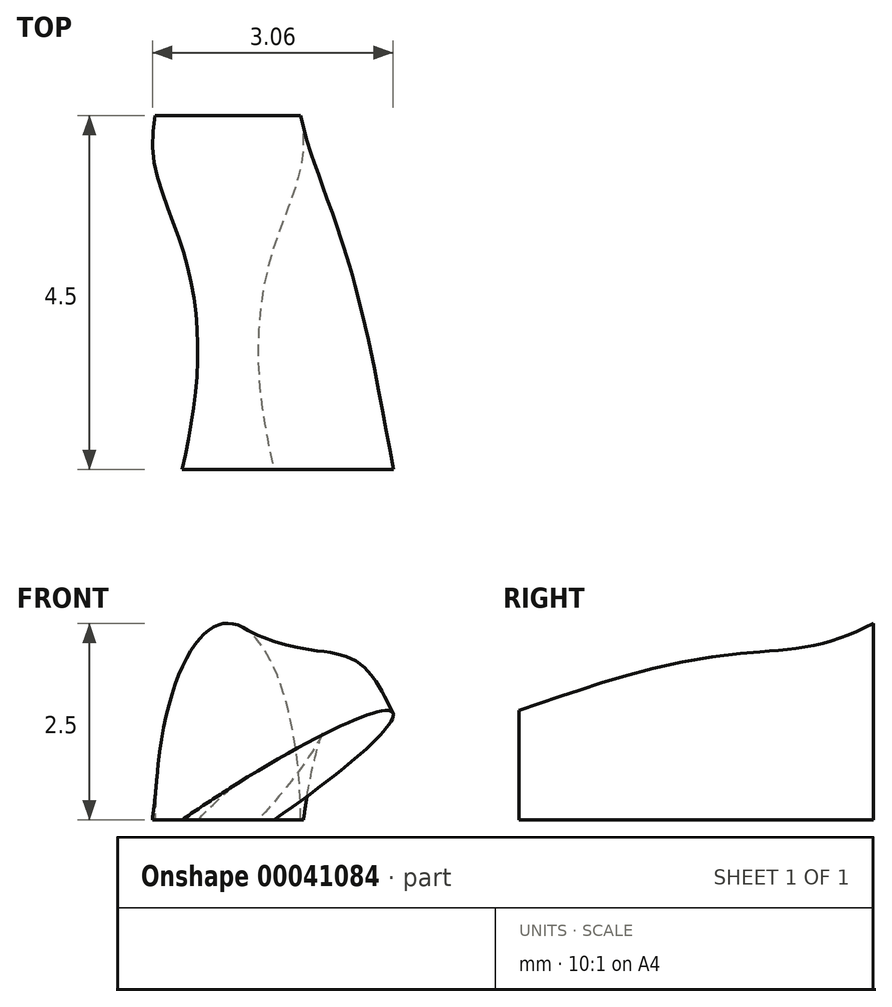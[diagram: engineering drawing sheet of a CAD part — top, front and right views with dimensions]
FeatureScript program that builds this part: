
annotation { "Feature Type Name" : "Feature", "Feature Type Description" : "" }
export const myFeature = defineFeature(function(context is Context, id is Id, definition is map)
    precondition{}
    {
        {
            var Q0;
            Q0=qCreatedBy(makeId("Front.planeOp"),FACE);
            cPlane(context, id + "F0", {"entities" : qUnion([Q0]), "cplaneType" : CPlaneType.OFFSET, "offset" : 1.5 * mm, "width" : 150 * mm, "height" : 150 * mm});
        }
        {
            var Q0;
            Q0=qCreatedBy(makeId("Front.planeOp"),FACE);
            cPlane(context, id + "F1", {"entities" : qUnion([Q0]), "cplaneType" : CPlaneType.OFFSET, "offset" : 4.5 * mm, "width" : 150 * mm, "height" : 150 * mm});
        }
        {
            var Q0;
            Q0=qCreatedBy(makeId("Front.planeOp"),FACE);
            var sketch = newSketch(context, id + "F2", { "sketchPlane" : qUnion([Q0])});
            skEllipse(sketch, "E0", {"center": v(0, 0) * mm, "majorRadius": 2.5 * mm, "minorRadius": 0.92 * mm, "majorAxis": v(0, 1)});
            skSolve(sketch);
        }
        {
            var Q0;
            Q0=qCreatedBy(id+"F0.planeOp",FACE);
            var sketch = newSketch(context, id + "F3", { "sketchPlane" : qUnion([Q0])});
            skEllipse(sketch, "E1", {"center": v(0, 0) * mm, "majorRadius": 2.5 * mm, "minorRadius": 0.55 * mm, "majorAxis": v(0.54, 0.84)});
            skSolve(sketch);
        }
        {
            var Q0;
            Q0=qCreatedBy(id+"F1.planeOp",FACE);
            var sketch = newSketch(context, id + "F4", { "sketchPlane" : qUnion([Q0])});
            skEllipse(sketch, "E2", {"center": v(0, 0) * mm, "majorRadius": 2.5 * mm, "minorRadius": 0.33 * mm, "majorAxis": v(0.84, 0.55)});
            skSolve(sketch);
        }
        {
            var Q0;
            Q0=makeQuery(id+"F2.imprint","IMPRINT",FACE,{"disambiguationData":[TD([[makeQuery(id+"F2.imprint","IMPRINT",EDGE,{"derivedFrom":sQuery(id+"F2.wireOp",EDGE,"E0")}),1.0]])]});
            var Q1;
            Q1=makeQuery(id+"F3.imprint","IMPRINT",FACE,{"disambiguationData":[TD([[makeQuery(id+"F3.imprint","IMPRINT",EDGE,{"derivedFrom":sQuery(id+"F3.wireOp",EDGE,"E1")}),1.0]])]});
            var Q2;
            Q2=makeQuery(id+"F4.imprint","IMPRINT",FACE,{"disambiguationData":[TD([[makeQuery(id+"F4.imprint","IMPRINT",EDGE,{"derivedFrom":sQuery(id+"F4.wireOp",EDGE,"E2")}),1.0]])]});
            loft(context, id + "F5", {"sheetProfilesArray" : [{ "sheetProfileEntities" : qUnion([Q0]) }, { "sheetProfileEntities" : qUnion([Q1]) }, { "sheetProfileEntities" : qUnion([Q2]) }]});
        }
        {
            var Q0;
            Q0=qCreatedBy(makeId("Top.planeOp"),FACE);
            var sketch = newSketch(context, id + "F6", { "sketchPlane" : qUnion([Q0])});
            skLineSegment(sketch, "E3.bottom", {"start": v(-4.44, 6.06) * mm, "end": v(8.21, 6.06) * mm});
            skLineSegment(sketch, "E3.top", {"start": v(-4.44, -16.54) * mm, "end": v(8.21, -16.54) * mm});
            skLineSegment(sketch, "E3.left", {"start": v(-4.44, 6.06) * mm, "end": v(-4.44, -16.54) * mm});
            skLineSegment(sketch, "E3.right", {"start": v(8.21, 6.06) * mm, "end": v(8.21, -16.54) * mm});
            skSolve(sketch);
        }
        {
            var Q0;
            Q0=makeQuery(id+"F6.imprint","IMPRINT",FACE,{"disambiguationData":[TD([[makeQuery(id+"F6.imprint","IMPRINT",EDGE,{"derivedFrom":sQuery(id+"F6.wireOp",EDGE,"E3.bottom")}),-1.0]])]});
            extrude(context, id + "F7", {"entities" : qUnion([Q0]), "operationType" : NewBodyOperationType.REMOVE, "oppositeDirection" : true, "depth" : 25 * mm});
        }
    });
